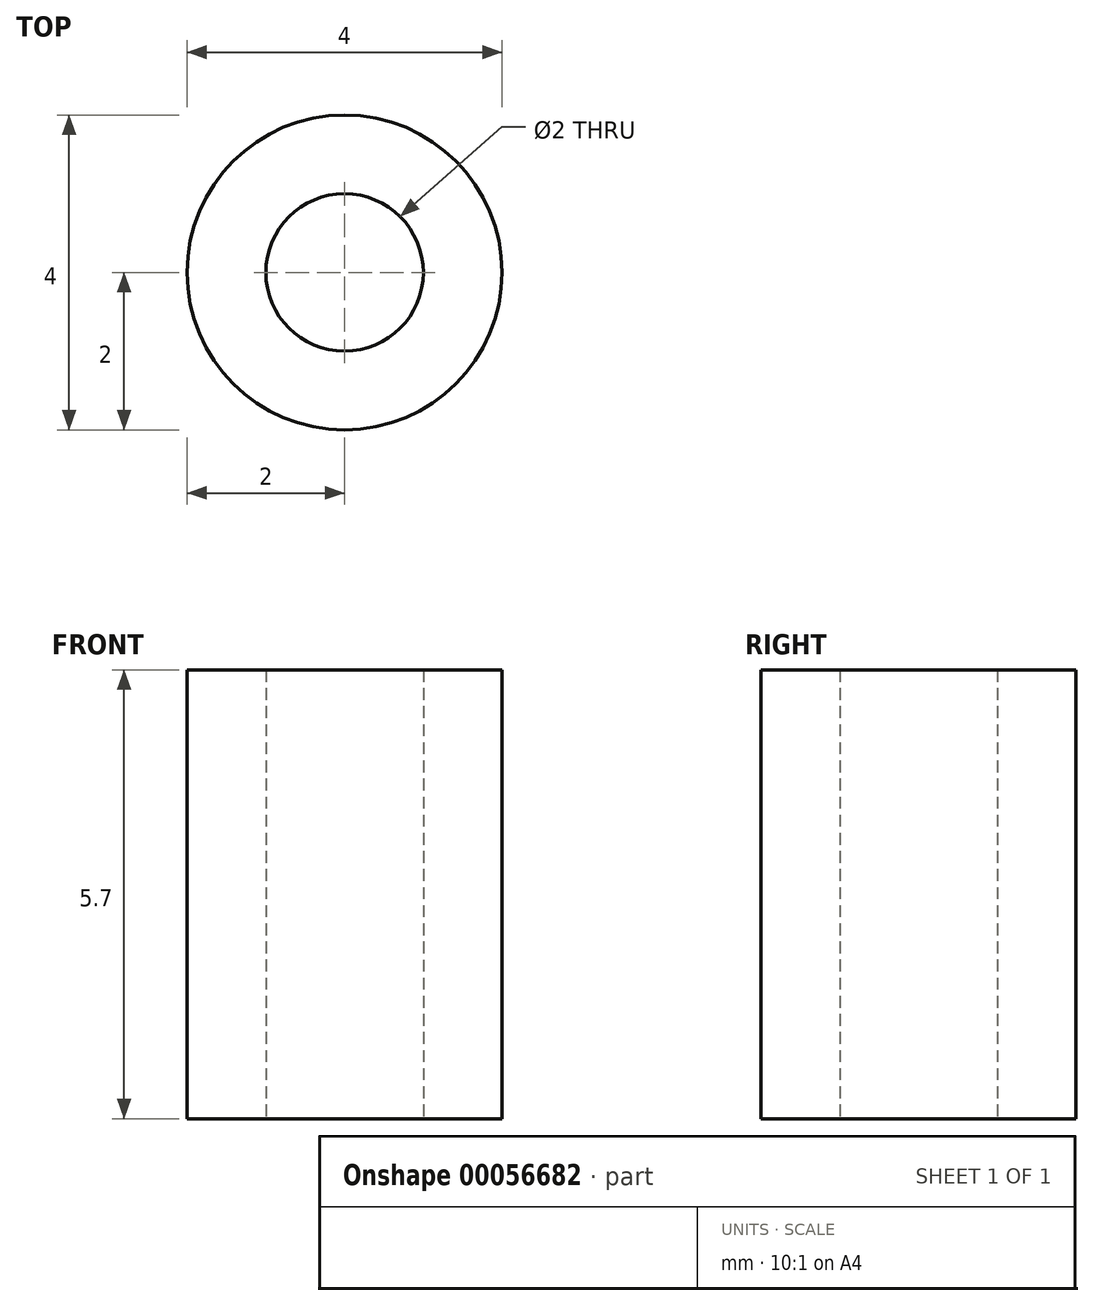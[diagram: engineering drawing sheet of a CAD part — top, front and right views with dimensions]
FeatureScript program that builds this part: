
annotation { "Feature Type Name" : "Feature", "Feature Type Description" : "" }
export const myFeature = defineFeature(function(context is Context, id is Id, definition is map)
    precondition{}
    {
        {
            var Q0;
            Q0=qCreatedBy(makeId("Top.planeOp"),FACE);
            var sketch = newSketch(context, id + "F0", { "sketchPlane" : qUnion([Q0])});
            skCircle(sketch, "E0", {"center": v(0, 0) * mm, "radius": 1 * mm});
            skCircle(sketch, "E1", {"center": v(0, 0) * mm, "radius": 2 * mm});
            skSolve(sketch);
        }
        {
            var Q0;
            Q0 = qSketchRegion(id + "F0", true);
            extrude(context, id + "F1", {"entities" : qUnion([Q0]), "depth" : 5.7 * mm});
        }
    });
